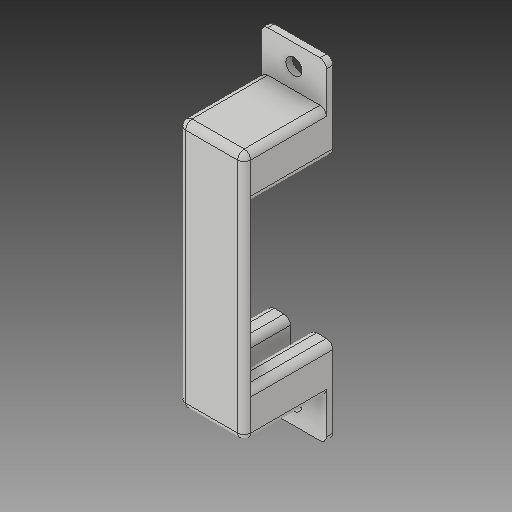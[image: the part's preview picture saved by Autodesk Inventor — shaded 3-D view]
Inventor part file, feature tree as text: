
AUTODESK INVENTOR PART (.ipt)
format: ipt  version: 2018 (Build 220112000, 112)  size: 247,808 bytes
history: native  units: mm
features: reference x7, other x6, extrude x5, sketch x5, fillet x4
ambient origin geometry x8: Origin, YZ Plane, XZ Plane, XY Plane, X Axis, Y Axis, Z Axis, Center Point
bodies: Solid1 (feature_tree)
feature tree (27):
  extrude  "Extrusion1"  Depth=0.25mm
  extrude  "Extrusion2"  Depth=3.5mm
  extrude  "Extrusion3"  Depth=1.0mm TaperAngle=0.0deg
  fillet  "Fillet2"  Radius=6.35mm
  extrude  "Extrusion4"  Depth=2.5mm
  fillet  "Fillet4"  Radius=2.5mm
  fillet  "Fillet5"  Radius=1.0mm
  fillet  "Fillet6"  Radius=1.0mm
  extrude  "Extrusion5"  Depth=10.0mm TaperAngle=0.0deg
  sketch  "Sketch1"  dims[d0=0.25mm d1=0.25mm]
  reference  "Reference1"
  reference  "Reference2"
  reference  "Reference3"
  reference  "Reference4"
  reference  "Reference5"
  sketch  "Sketch2"  dims[d2=3.5mm d3=3.0mm]
  sketch  "Sketch3"  dims[d4=12.7mm d5=0.0mm d6=1.0mm d7=0.0mm d8=6.35mm]
  sketch  "Sketch4"  dims[d9=6.35mm d10=2.5mm d11=2.5mm d12=1.0mm d13=0.0mm d15=1.0mm]
  reference  "Reference6"
  reference  "Reference7"
  sketch  "Sketch5"  dims[d17=1.0mm d18=10.0mm d19=0.0mm d20=1.0mm d21=1.0mm d22=1.0mm d23=1.0mm d24=0.5mm d25=10.0mm d26=0.0mm]
  other  "<userpath>\OneDrive\Documents\Inventor\TSA\2018\Animatronics\Tortoise\AssemblyTURTLE.iam"
  other  "AssemblyTURTLE.iam"
  other  "Servo_With_Attachment:1"
  other  "<userpath>\OneDrive\Documents\Inventor\TSA\2018\Animatronics\Tortoise\TurtleAssembly.iam"
  other  "TurtleAssembly.iam"
  other  "servo (2):3"
